# Revit family: CADS_AIRFLOWdev_Airvalve_PlasticAdjustable_Extract
name_source: partatom
category: Air Terminals
revit_build: Autodesk Revit 2015 (Build: 20160512_1515(x64)
units: mm (PartAtom-declared; Revit-internal decimal feet)

## types (4) — shared parameters
6MonthlyMaintenance = Visually inspect system, clean the fan and ducting if necessary
AssemblyPlace = UNKNOWN
AssetType = FIXED
B1 = 20 mm  [stored 0.0656168 ft]
CEApproval = Yes
Color = White
Default Elevation = 1219 mm
DurationUnit = Year
ExpectedServiceLife = 10
Finish = Lacquer
FireControlPanelLinks = No
Fitting Type = Ignore
Grade = Virgin
ISO140001 = Yes
ISO90001 = Yes
IsExtendedWarranty = No
Manufacturer = Airflow Developments Ltd
ManufacturerAddress = Aidelle House
Lancaster Road
Cressex Business Park
High Wycombe
Bucks
HP123QP
ManufacturerTelephone = 01494 525252
ManufacturerWebsite = www.airflow.com
Material = Plastic
NBSCode = 90-75-50/370 Air terminals;
PassiveHouseApproval = No
PointOfContact = Airflow Developments Ltd
ProductLiterature = https://www.airflow.com
ProductionYear = 2017
Quantity = 1
RedDotDesignAward = No
RunID = 0
SAPApproval = Yes
ServiceLifeDuration = 10
ServiceLifeType = EXPECTEDSERVICELIFE
Shape = Round
Status = New
TemperatureRange = up to 40°C
Uniclass2015 = Pr_65_70_46_07
WarrantyGuarantor = Airflow Developments Ltd
WarrantyPeriod = 0
zero-valued in all types: CADS_Index

## per-type parameters (varying)
| type | A | A1 | B | Constituents | DuctDiameter | Features | GrossWeight | NominalHeight | NominalLength | NominalWidth | ReplacementCost | ShippingWeight | Size |
| 100mm | 140 mm | 75 mm | 60 mm | Plastic Adjustable Air Valve Supply 100mm Dia | 100 mm  [stored 0.328084 ft] | Plastic Adjustable Air Valve Supply 100mm Dia | 0.20 kg | 60 mm | 140 mm | 140 mm | 17.544 | 0.24 kg | 60 x 140 x 140 |
| 125mm | 165 mm | 100 mm  [stored 0.328084 ft] | 65 mm | Plastic Adjustable Air Valve Supply 125mm Dia | 125 mm | Plastic Adjustable Air Valve Supply 125mm Dia | 0.22 kg | 65 mm | 165 mm | 165 mm | 19.14 | 0.26 kg | 65 x 165 x 165 |
| 150mm | 185 mm | 125 mm | 55 mm | Plastic Adjustable Air Valve Supply 150mm Dia | 150 mm | Plastic Adjustable Air Valve Supply 150mm Dia | 0.25 kg | 55 mm | 185 mm | 185 mm | 27.564 | 0.30 kg | 55 x 185 x 185 |
| 200mm | 245 mm  [stored 0.803806 ft] | 175 mm  [stored 0.574147 ft] | 80 mm  [stored 0.262467 ft] | Plastic Adjustable Air Valve Supply 200mm Dia | 200 mm  [stored 0.656168 ft] | Plastic Adjustable Air Valve Supply 200mm Dia | 0.25 kg | 80 mm  [stored 0.262467 ft] | 245 mm  [stored 0.803806 ft] | 245 mm  [stored 0.803806 ft] | 29.448 | 0.30 kg | 80 x 245 x 245 |

note: [stored X ft] marks values corroborated as IEEE doubles in the binary element streams (Revit-internal decimal feet)

## geometry (parser evidence)
native form markers: Blend x4, Sweep x2
no freeform markers — native parametric forms only
